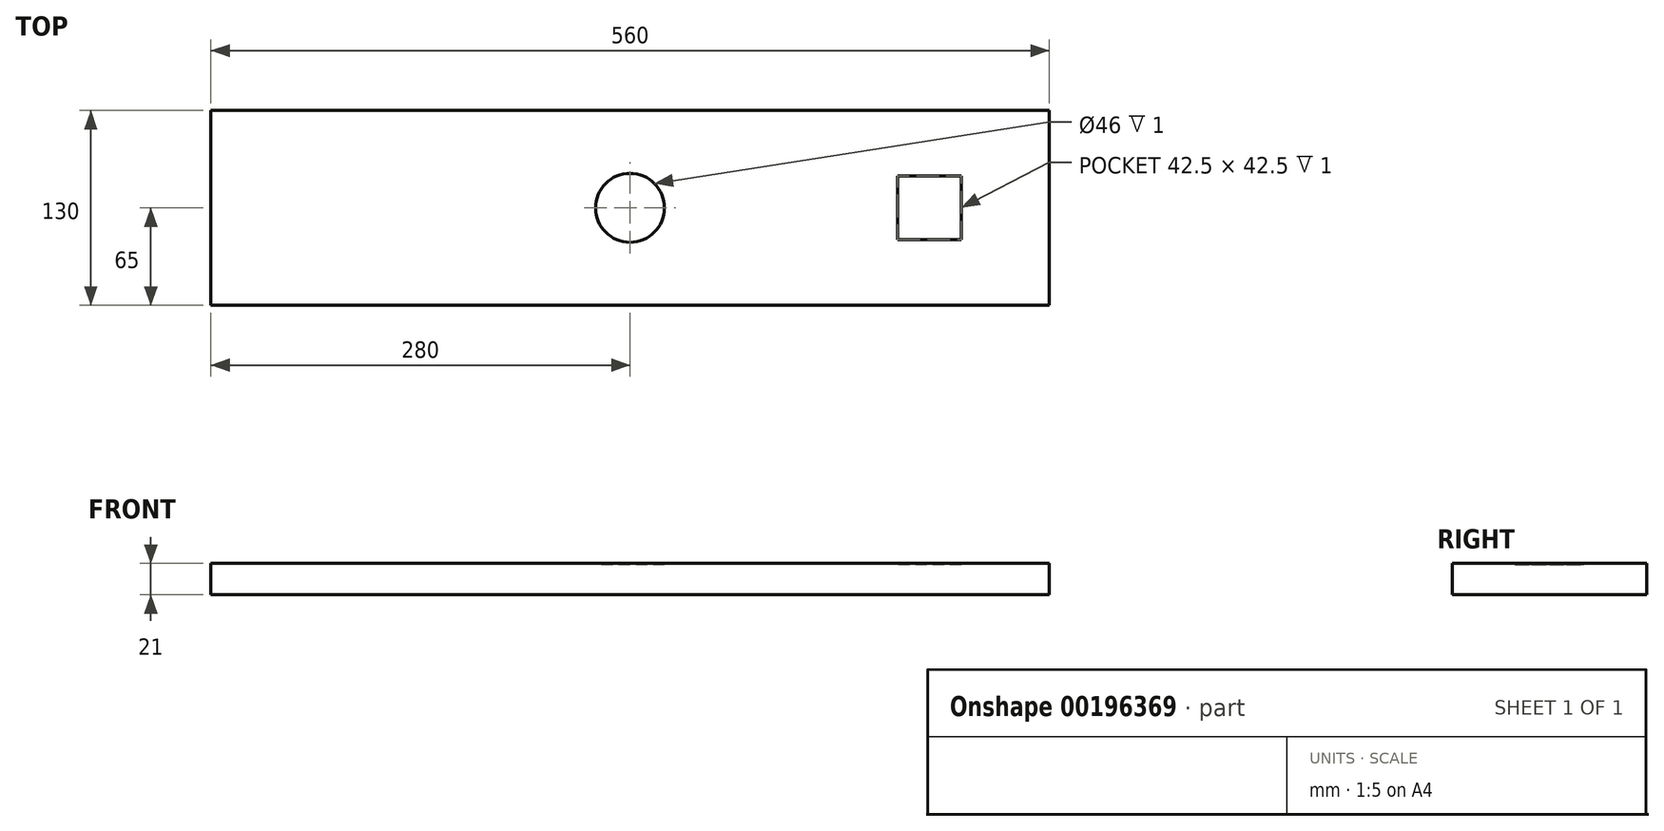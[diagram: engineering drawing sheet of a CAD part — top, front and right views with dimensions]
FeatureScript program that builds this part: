
annotation { "Feature Type Name" : "Feature", "Feature Type Description" : "" }
export const myFeature = defineFeature(function(context is Context, id is Id, definition is map)
    precondition{}
    {
        {
            var Q0;
            Q0=qCreatedBy(makeId("Top.planeOp"),FACE);
            var sketch = newSketch(context, id + "F0", { "sketchPlane" : qUnion([Q0])});
            skLineSegment(sketch, "E0.bottom", {"start": v(0, 0) * mm, "end": v(560, 0) * mm});
            skLineSegment(sketch, "E0.top", {"start": v(0, 130) * mm, "end": v(560, 130) * mm});
            skLineSegment(sketch, "E0.left", {"start": v(0, 0) * mm, "end": v(0, 130) * mm});
            skLineSegment(sketch, "E0.right", {"start": v(560, 0) * mm, "end": v(560, 130) * mm});
            skSolve(sketch);
        }
        {
            var Q0;
            Q0 = qSketchRegion(id + "F0", true);
            extrude(context, id + "F1", {"entities" : qUnion([Q0]), "depth" : 21 * mm});
        }
        {
            var Q0;
            Q0=makeQuery(id+"F1.opExtrude","CAP_FACE",FACE,{"disambiguationData":[OSD([sQuery(id+"F0.wireOp",EDGE,"E0.bottom"),sQuery(id+"F0.wireOp",EDGE,"E0.top"),sQuery(id+"F0.wireOp",EDGE,"E0.left"),sQuery(id+"F0.wireOp",EDGE,"E0.right")])],"isStart":false});
            var sketch = newSketch(context, id + "F2", { "sketchPlane" : qUnion([Q0])});
            skLineSegment(sketch, "E1", {"start": v(280, 0) * mm, "end": v(280, 130) * mm, "construction": true});
            skLineSegment(sketch, "E2.bottom", {"start": v(560, 0) * mm, "end": v(0, 0) * mm, "construction": true});
            skLineSegment(sketch, "E2.top", {"start": v(560, 130) * mm, "end": v(0, 130) * mm, "construction": true});
            skLineSegment(sketch, "E2.left", {"start": v(560, 0) * mm, "end": v(560, 130) * mm, "construction": true});
            skLineSegment(sketch, "E2.right", {"start": v(0, 0) * mm, "end": v(0, 130) * mm, "construction": true});
            skLineSegment(sketch, "E3.trimOffspring", {"start": v(280, 65) * mm, "end": v(0, 65) * mm, "construction": true});
            skLineSegment(sketch, "E4", {"start": v(280, 65) * mm, "end": v(560, 65) * mm, "construction": true});
            skLineSegment(sketch, "E5", {"start": v(480, 0) * mm, "end": v(480, 86.25) * mm, "construction": true});
            skPoint(sketch, "E5.startSnap0", {"position": v(480, 43.75) * mm});
            skLineSegment(sketch, "E6", {"start": v(480, 86.25) * mm, "end": v(480, 130) * mm, "construction": true});
            skCircle(sketch, "E7", {"center": v(280, 65) * mm, "radius": 23 * mm});
            skPoint(sketch, "E8", {"position": v(480, 65) * mm});
            skLineSegment(sketch, "E9.bottom", {"start": v(501.25, 43.75) * mm, "end": v(458.75, 43.75) * mm});
            skLineSegment(sketch, "E9.top", {"start": v(501.25, 86.25) * mm, "end": v(458.75, 86.25) * mm});
            skLineSegment(sketch, "E9.left", {"start": v(501.25, 43.75) * mm, "end": v(501.25, 86.25) * mm});
            skLineSegment(sketch, "E9.right", {"start": v(458.75, 43.75) * mm, "end": v(458.75, 86.25) * mm});
            skSolve(sketch);
        }
        {
            var Q0;
            Q0 = qSketchRegion(id + "F2", true);
            extrude(context, id + "F3", {"entities" : qUnion([Q0]), "operationType" : NewBodyOperationType.REMOVE, "oppositeDirection" : true, "depth" : 1 * mm});
        }
    });
